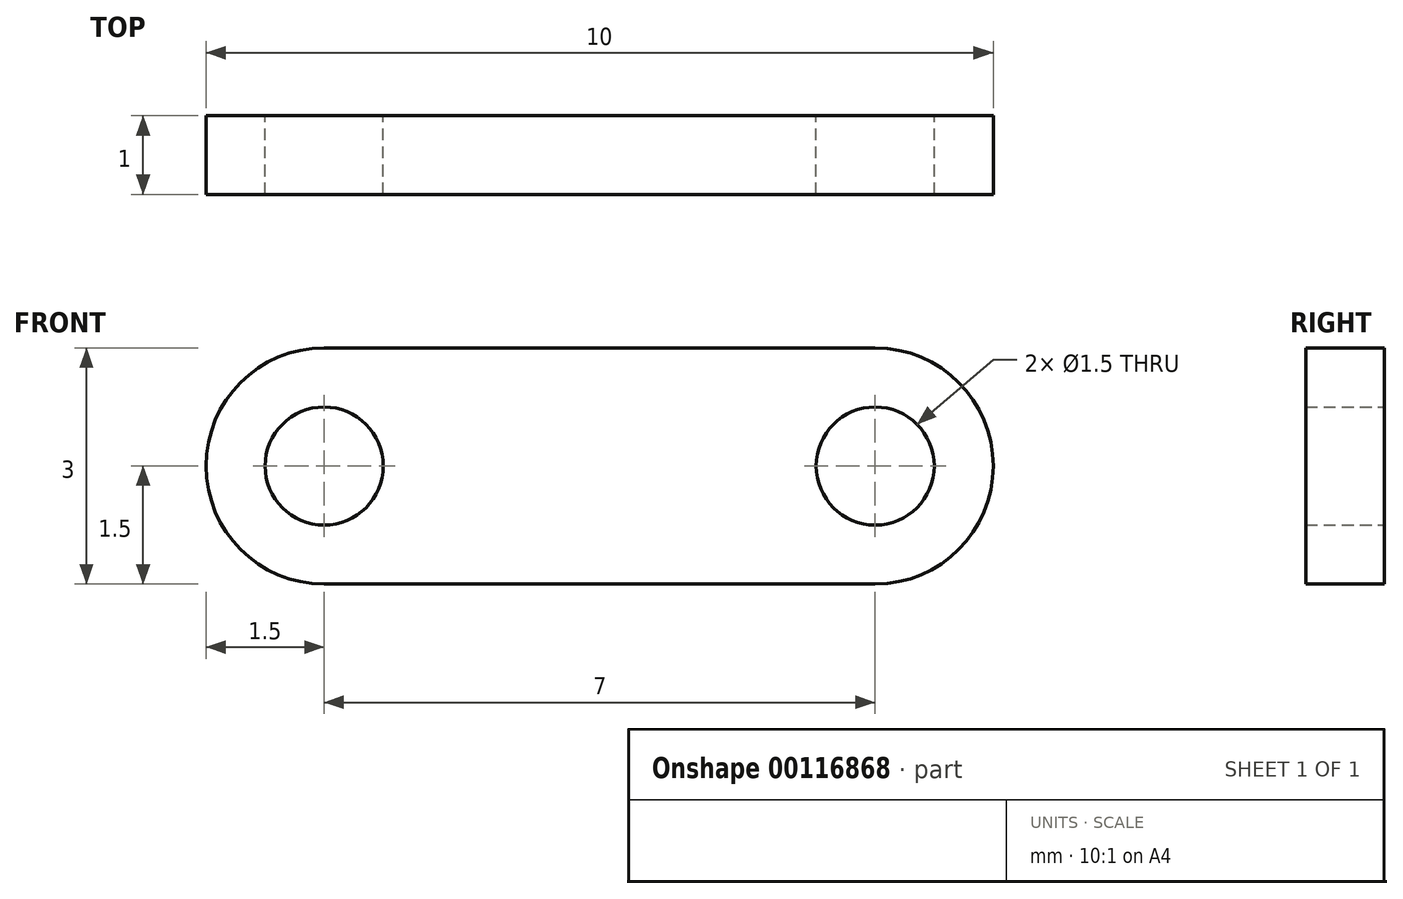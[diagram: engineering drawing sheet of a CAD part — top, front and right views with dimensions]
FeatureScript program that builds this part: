
annotation { "Feature Type Name" : "Feature", "Feature Type Description" : "" }
export const myFeature = defineFeature(function(context is Context, id is Id, definition is map)
    precondition{}
    {
        {
            var Q0;
            Q0=qCreatedBy(makeId("Front.planeOp"),FACE);
            var sketch = newSketch(context, id + "F0", { "sketchPlane" : qUnion([Q0])});
            skLineSegment(sketch, "E0.bottom", {"start": v(-3.5, 1.5) * mm, "end": v(3.5, 1.5) * mm});
            skLineSegment(sketch, "E0.top", {"start": v(-3.5, -1.5) * mm, "end": v(3.5, -1.5) * mm});
            skLineSegment(sketch, "E0.left", {"start": v(-3.5, 1.5) * mm, "end": v(-3.5, -1.5) * mm});
            skLineSegment(sketch, "E0.right", {"start": v(3.5, 1.5) * mm, "end": v(3.5, -1.5) * mm});
            skArc(sketch, "E1", {"start": v(-3.5, 1.5) * mm, "mid": v(-5, 0) * mm, "end": v(-3.5, -1.5) * mm});
            skArc(sketch, "E2", {"start": v(3.5, -1.5) * mm, "mid": v(5, 0) * mm, "end": v(3.5, 1.5) * mm});
            skCircle(sketch, "E3", {"center": v(-3.5, 0) * mm, "radius": 0.75 * mm});
            skCircle(sketch, "E4.MirrorC", {"center": v(3.5, 0) * mm, "radius": 0.75 * mm});
            skSolve(sketch);
        }
        {
            var Q0;
            {var subQ0=sQuery(id+"F0.wireOp",EDGE,"E1");Q0=makeQuery(id+"F0.imprint","IMPRINT",FACE,{"disambiguationData":[TD([[makeQuery(id+"F0.imprint","IMPRINT",EDGE,{"derivedFrom":subQ0}),1.0]])]});}
            var Q1;
            {var subQ0=sQuery(id+"F0.wireOp",EDGE,"E2");Q1=makeQuery(id+"F0.imprint","IMPRINT",FACE,{"disambiguationData":[TD([[makeQuery(id+"F0.imprint","IMPRINT",EDGE,{"derivedFrom":subQ0}),1.0]])]});}
            var Q2;
            {var subQ5=sQuery(id+"F0.wireOp",EDGE,"E0.bottom");Q2=makeQuery(id+"F0.imprint","IMPRINT",FACE,{"disambiguationData":[TD([[makeQuery(id+"F0.imprint","IMPRINT",EDGE,{"derivedFrom":subQ5}),-1.0]])]});}
            extrude(context, id + "F1", {"entities" : qUnion([Q0, Q1, Q2]), "endBound" : BoundingType.SYMMETRIC, "depth" : 1 * mm});
        }
    });
